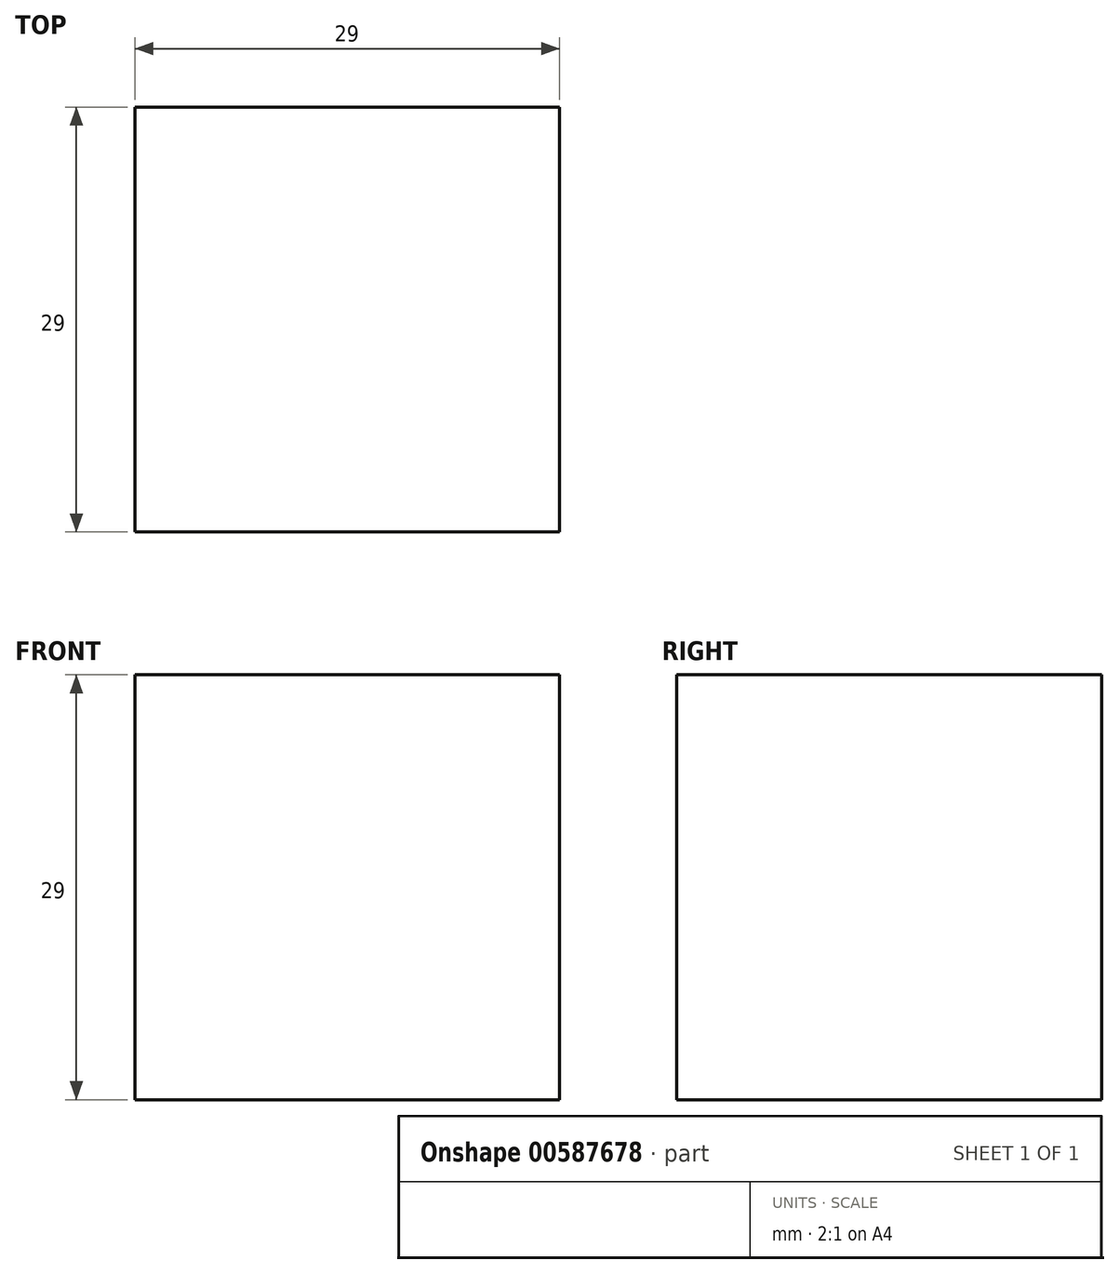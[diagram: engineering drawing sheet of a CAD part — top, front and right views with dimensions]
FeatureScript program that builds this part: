
annotation { "Feature Type Name" : "Feature", "Feature Type Description" : "" }
export const myFeature = defineFeature(function(context is Context, id is Id, definition is map)
    precondition{}
    {
        {
            var Q0;
            Q0=qCreatedBy(makeId("Front.planeOp"),FACE);
            var sketch = newSketch(context, id + "F0", { "sketchPlane" : qUnion([Q0])});
            skLineSegment(sketch, "E0.bottom", {"start": v(0, 0) * mm, "end": v(29, 0) * mm});
            skLineSegment(sketch, "E0.top", {"start": v(0, 29) * mm, "end": v(29, 29) * mm});
            skLineSegment(sketch, "E0.left", {"start": v(0, 0) * mm, "end": v(0, 29) * mm});
            skLineSegment(sketch, "E0.right", {"start": v(29, 0) * mm, "end": v(29, 29) * mm});
            skSolve(sketch);
        }
        {
            var Q0;
            Q0 = qSketchRegion(id + "F0", true);
            extrude(context, id + "F1", {"entities" : qUnion([Q0]), "depth" : 29 * mm, "offsetDistance" : 25 * mm});
        }
    });
